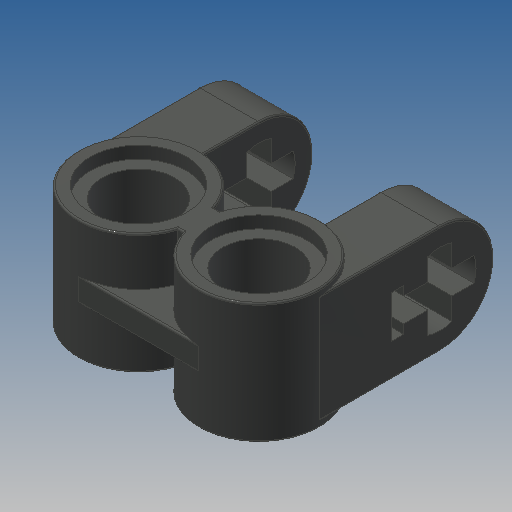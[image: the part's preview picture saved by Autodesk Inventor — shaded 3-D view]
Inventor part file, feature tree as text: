
AUTODESK INVENTOR PART (.ipt)
format: ipt  version: 2022.2 (Build 262287000, 287)  size: 312,320 bytes
history: native  units: mm
features: extrude x5, sketch x3, mirror x2, plane x1, fillet x1, projected_geometry x1
ambient origin geometry x8: Origin, YZ Plane, XZ Plane, XY Plane, X Axis, Y Axis, Z Axis, Center Point
bodies: Solid1 (feature_tree)
feature tree (13):
  sketch  "Sketch1"  dims[d0=8.0mm d2=8.0mm]
  extrude  "Extrusion1"  Depth=8.0mm
  extrude  "Extrusion13"  Depth=6.4mm
  plane  "Work Plane1"
  extrude  "Extrusion4"  Depth=0.1mm TaperAngle=0.0deg
  mirror  "Mirror2"
  extrude  "Extrusion14"  Depth=0.1mm
  mirror  "Mirror1"
  extrude  "Extrusion15"  Depth=0.1mm TaperAngle=0.0deg
  fillet  "Fillet1"  Radius=0.8mm
  sketch  "Sketch3"  dims[d3=4.8mm d4=6.4mm]
  projected_geometry  "Projected Loop1"
  sketch  "Sketch10"  dims[d7=8.0mm d8=0.0mm d15=4.0mm d16=0.0mm d35=2.4mm d36=1.6mm d37=0.0mm d38=0.8mm d39=0.0mm d47=4.8mm d49=7.2mm d50=0.8mm d51=2.8mm d52=8.0mm d53=1.6mm d54=0.9mm d55=0.0mm d56=0.1mm]
